# Revit family: S-755
name_source: partatom
category: Aparatos sanitarios
revit_build: Autodesk Revit 2015 (Build: 20140606_1530(x64)
units: mm (PartAtom-declared; Revit-internal decimal feet)

## types (6) — shared parameters
B = 52 mm
Comentarios de tipo = COMPATIBLE CON CERCOS VISTOS Y OCULTOS
Descripción = REJILLA PARA CANALETA, SPRING, PARA CANALETAS ANCHO 50
Fabricante = Jimten
Material = INOX AISI304
Modelo = S-755
Rejilla = INOX AISI304
URL = http://www.jimten.com
zero-valued in all types: CWFU

## per-type parameters (varying)
| type | A | DistExt | Medida | N_MatrizHuecos | Referencia |
| 50x350mm_SPRING | 340 mm | 10 mm  [stored 0.0328084 ft] | 350mm x 50mm | 2 | 13538 |
| 50x550mm_SPRING | 540 mm | 20 mm  [stored 0.0656168 ft] | 550mm x 50mm | 3 | 13558 |
| 50x650mm_SPRING | 640 mm  [stored 2.09974 ft] | 50 mm | 650mm x 50mm | 3 | 13568 |
| 50x750mm_SPRING | 740 mm  [stored 2.42782 ft] | 20 mm  [stored 0.0656168 ft] | 750mm x 50mm | 4 | 13578 |
| 50x850mm_SPRING | 840 mm | 10 mm  [stored 0.0328084 ft] | 850mm x 50mm | 5 | 13588 |
| 50x950mm_SPRING | 940 mm | 25 mm  [stored 0.082021 ft] | 950mm x 50mm | 5 | 13598 |

note: [stored X ft] marks values corroborated as IEEE doubles in the binary element streams (Revit-internal decimal feet)

## geometry (parser evidence)
native form markers: Blend x3, Sweep x2
no freeform markers — native parametric forms only
